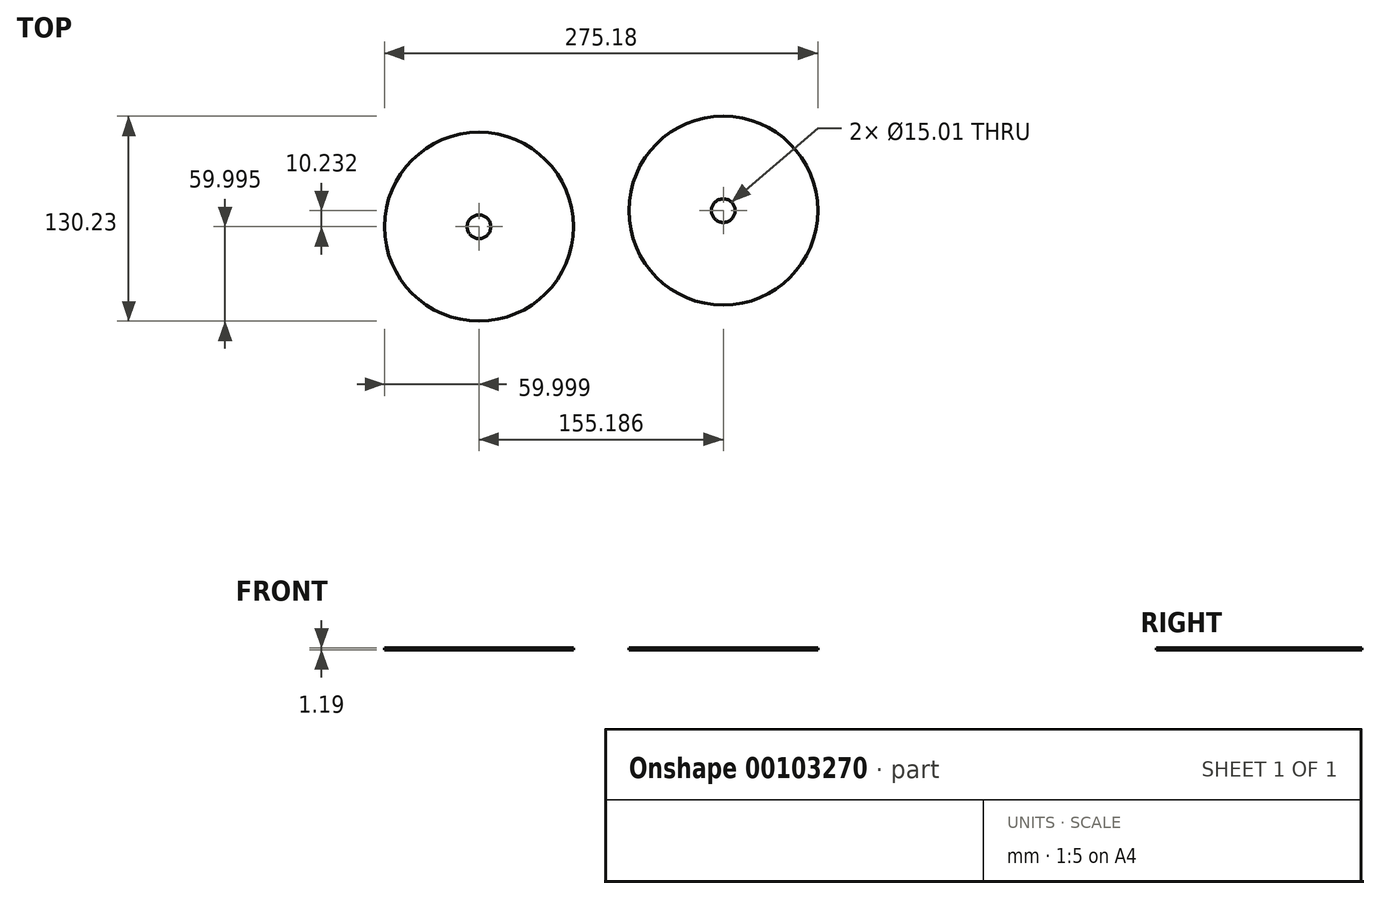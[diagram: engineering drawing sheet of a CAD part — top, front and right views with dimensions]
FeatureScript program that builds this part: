
annotation { "Feature Type Name" : "Feature", "Feature Type Description" : "" }
export const myFeature = defineFeature(function(context is Context, id is Id, definition is map)
    precondition{}
    {
        {
            var Q0;
            Q0=qCreatedBy(makeId("Top.planeOp"),FACE);
            var sketch = newSketch(context, id + "F0", { "sketchPlane" : qUnion([Q0])});
            skCircle(sketch, "E0", {"center": v(-74.47, 18.87) * mm, "radius": 60 * mm});
            skCircle(sketch, "E1", {"center": v(80.71, 29.1) * mm, "radius": 60 * mm});
            skSolve(sketch);
        }
        {
            var Q0;
            Q0 = qSketchRegion(id + "F0", true);
            extrude(context, id + "F1", {"entities" : qUnion([Q0]), "depth" : 1.2 * mm});
        }
        {
            var Q0;
            Q0=sQuery(id+"F0.wireOp",VERTEX,"E0.center");
            var Q1;
            Q1=sQuery(id+"F0.wireOp",VERTEX,"E1.center");
            var Q2;
            Q2=makeQuery(id+"F1.opExtrude","SWEPT_BODY",BODY,{"disambiguationData":[OSD([sQuery(id+"F0.wireOp",EDGE,"E0")])]});
            var Q3;
            Q3=makeQuery(id+"F1.opExtrude","SWEPT_BODY",BODY,{"disambiguationData":[OSD([sQuery(id+"F0.wireOp",EDGE,"E1")])]});
            hole(context, id + "F2", {"style" : HoleStyle.SIMPLE, "endStyle" : HoleEndStyle.THROUGH, "oppositeDirection" : true, "holeDiameter" : 15 * mm, "locations" : qUnion([Q0, Q1]), "scope" : qUnion([Q2, Q3]), "isTappedThrough" : true});
        }
    });
